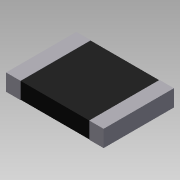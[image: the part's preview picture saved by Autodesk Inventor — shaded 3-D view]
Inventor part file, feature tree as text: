
AUTODESK INVENTOR PART (.ipt)
format: ipt  version: 2011 (Build 150239000, 239)  size: 113,152 bytes
history: native  units: mm
features: extrude x5, sketch x5, other x1
ambient origin geometry x8: Origin, YZ Plane, XZ Plane, XY Plane, X Axis, Y Axis, Z Axis, Center Point
feature tree (11):
  other  "Твердое тело1"
  extrude  "Выдавливание1"  Depth=3.41mm
  extrude  "Выдавливание2"  Depth=4.73mm
  extrude  "Выдавливание3"  Depth=2.365mm
  extrude  "Выдавливание4"  Depth=1.705mm
  extrude  "Выдавливание5"  Depth=0.81mm TaperAngle=0.0deg
  sketch  "Эскиз1"
  sketch  "Эскиз2"
  sketch  "Эскиз3"
  sketch  "Эскиз4"
  sketch  "Эскиз5"
